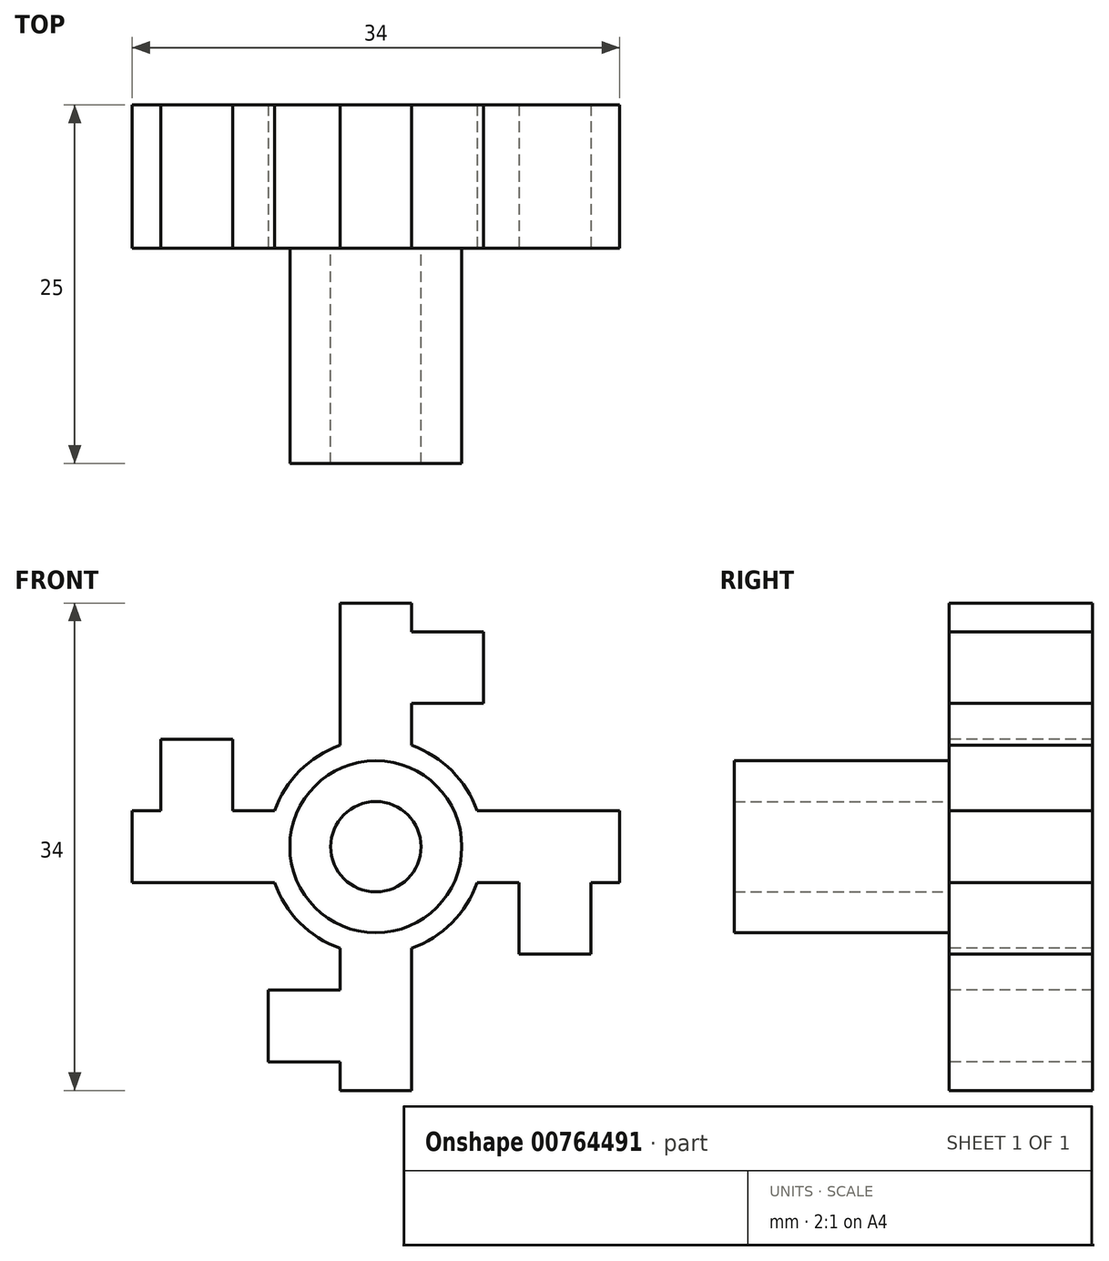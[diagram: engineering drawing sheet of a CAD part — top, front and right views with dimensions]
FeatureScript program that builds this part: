
annotation { "Feature Type Name" : "Feature", "Feature Type Description" : "" }
export const myFeature = defineFeature(function(context is Context, id is Id, definition is map)
    precondition{}
    {
        {
            var Q0;
            Q0=qCreatedBy(makeId("Front.planeOp"),FACE);
            var sketch = newSketch(context, id + "F0", { "sketchPlane" : qUnion([Q0])});
            skCircle(sketch, "E0", {"center": v(0, 0) * mm, "radius": 3.15 * mm});
            skCircle(sketch, "E1", {"center": v(0, 0) * mm, "radius": 6 * mm});
            skSolve(sketch);
        }
        {
            var Q0;
            Q0=qCreatedBy(makeId("Front.planeOp"),FACE);
            var sketch = newSketch(context, id + "F1", { "sketchPlane" : qUnion([Q0])});
            skArc(sketch, "E2", {"start": v(-2.5, 7.07) * mm, "mid": v(-5.3, 5.3) * mm, "end": v(-7.07, 2.5) * mm});
            skLineSegment(sketch, "E3.left", {"start": v(2.5, 10) * mm, "end": v(2.5, 7.07) * mm});
            skLineSegment(sketch, "E3.right", {"start": v(-2.5, 12.5) * mm, "end": v(-2.5, 7.07) * mm});
            skPoint(sketch, "E3.middle", {"position": v(0, 7.5) * mm});
            skLineSegment(sketch, "E4.bottom", {"start": v(7.5, 10) * mm, "end": v(2.5, 10) * mm});
            skLineSegment(sketch, "E4.top", {"start": v(7.5, 15) * mm, "end": v(2.5, 15) * mm});
            skLineSegment(sketch, "E4.left", {"start": v(7.5, 10) * mm, "end": v(7.5, 15) * mm});
            skLineSegment(sketch, "E4.right", {"start": v(-2.5, 12.5) * mm, "end": v(-2.5, 15) * mm});
            skPoint(sketch, "E4.middle", {"position": v(2.5, 12.5) * mm});
            skPoint(sketch, "E3.top.end.orphan", {"position": v(-2.5, 2.5) * mm});
            skPoint(sketch, "E5.orphan", {"position": v(2.5, 2.5) * mm});
            skPoint(sketch, "E6.orphan", {"position": v(-2.5, 10) * mm});
            skLineSegment(sketch, "E7", {"start": v(-2.5, 15) * mm, "end": v(-2.5, 17) * mm});
            skLineSegment(sketch, "E8", {"start": v(-2.5, 17) * mm, "end": v(2.5, 17) * mm});
            skLineSegment(sketch, "E9", {"start": v(2.5, 17) * mm, "end": v(2.5, 15) * mm});
            skLineSegment(sketch, "E10.1.0", {"start": v(-12.5, -2.5) * mm, "end": v(-7.07, -2.5) * mm});
            skLineSegment(sketch, "E10.1.1", {"start": v(-12.5, -2.5) * mm, "end": v(-15, -2.5) * mm});
            skLineSegment(sketch, "E10.1.2", {"start": v(-15, -2.5) * mm, "end": v(-17, -2.5) * mm});
            skLineSegment(sketch, "E10.1.3", {"start": v(-17, -2.5) * mm, "end": v(-17, 2.5) * mm});
            skLineSegment(sketch, "E10.1.4", {"start": v(-17, 2.5) * mm, "end": v(-15, 2.5) * mm});
            skLineSegment(sketch, "E10.1.5", {"start": v(-15, 7.5) * mm, "end": v(-15, 2.5) * mm});
            skLineSegment(sketch, "E10.1.6", {"start": v(-10, 7.5) * mm, "end": v(-15, 7.5) * mm});
            skLineSegment(sketch, "E10.1.7", {"start": v(-10, 7.5) * mm, "end": v(-10, 2.5) * mm});
            skLineSegment(sketch, "E10.1.8", {"start": v(-10, 2.5) * mm, "end": v(-7.07, 2.5) * mm});
            skLineSegment(sketch, "E10.2.0", {"start": v(2.5, -12.5) * mm, "end": v(2.5, -7.07) * mm});
            skLineSegment(sketch, "E10.2.1", {"start": v(2.5, -12.5) * mm, "end": v(2.5, -15) * mm});
            skLineSegment(sketch, "E10.2.2", {"start": v(2.5, -15) * mm, "end": v(2.5, -17) * mm});
            skLineSegment(sketch, "E10.2.3", {"start": v(2.5, -17) * mm, "end": v(-2.5, -17) * mm});
            skLineSegment(sketch, "E10.2.4", {"start": v(-2.5, -17) * mm, "end": v(-2.5, -15) * mm});
            skLineSegment(sketch, "E10.2.5", {"start": v(-7.5, -15) * mm, "end": v(-2.5, -15) * mm});
            skLineSegment(sketch, "E10.2.6", {"start": v(-7.5, -10) * mm, "end": v(-7.5, -15) * mm});
            skLineSegment(sketch, "E10.2.7", {"start": v(-7.5, -10) * mm, "end": v(-2.5, -10) * mm});
            skLineSegment(sketch, "E10.2.8", {"start": v(-2.5, -10) * mm, "end": v(-2.5, -7.07) * mm});
            skLineSegment(sketch, "E11.2.3.0", {"start": v(12.5, 2.5) * mm, "end": v(7.07, 2.5) * mm});
            skLineSegment(sketch, "E11.3.3.0", {"start": v(12.5, 2.5) * mm, "end": v(15, 2.5) * mm});
            skLineSegment(sketch, "E11.6.3.0", {"start": v(15, 2.5) * mm, "end": v(17, 2.5) * mm});
            skLineSegment(sketch, "E11.9.3.0", {"start": v(17, 2.5) * mm, "end": v(17, -2.5) * mm});
            skLineSegment(sketch, "E11.12.3.0", {"start": v(17, -2.5) * mm, "end": v(15, -2.5) * mm});
            skLineSegment(sketch, "E11.15.3.0", {"start": v(15, -7.5) * mm, "end": v(15, -2.5) * mm});
            skLineSegment(sketch, "E11.18.3.0", {"start": v(10, -7.5) * mm, "end": v(15, -7.5) * mm});
            skLineSegment(sketch, "E11.21.3.0", {"start": v(10, -7.5) * mm, "end": v(10, -2.5) * mm});
            skLineSegment(sketch, "E11.24.3.0", {"start": v(10, -2.5) * mm, "end": v(7.07, -2.5) * mm});
            skArc(sketch, "E12.trimOffspring", {"start": v(-7.07, -2.5) * mm, "mid": v(-5.3, -5.3) * mm, "end": v(-2.5, -7.07) * mm});
            skArc(sketch, "E13.trimOffspring", {"start": v(7.07, 2.5) * mm, "mid": v(5.3, 5.3) * mm, "end": v(2.5, 7.07) * mm});
            skArc(sketch, "E14.trimOffspring", {"start": v(2.5, -7.07) * mm, "mid": v(5.3, -5.3) * mm, "end": v(7.07, -2.5) * mm});
            skSolve(sketch);
        }
        {
            var Q0;
            Q0 = qSketchRegion(id + "F0", true);
            extrude(context, id + "F2", {"entities" : qUnion([Q0]), "depth" : 15 * mm, "offsetDistance" : 25 * mm});
        }
        {
            var Q0;
            Q0 = qSketchRegion(id + "F1", true);
            extrude(context, id + "F3", {"entities" : qUnion([Q0]), "operationType" : NewBodyOperationType.ADD, "depth" : 0 * mm, "offsetDistance" : 25 * mm, "hasSecondDirection" : true, "secondDirectionOppositeDirection" : true, "secondDirectionDepth" : 10 * mm});
        }
    });
